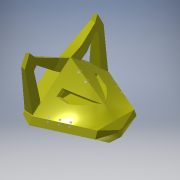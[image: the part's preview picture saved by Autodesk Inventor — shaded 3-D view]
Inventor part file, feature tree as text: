
AUTODESK INVENTOR PART (.ipt)
format: ipt  version: 2017 (Build 210142000, 142)  size: 774,144 bytes
history: native  units: in
note: dims shown in document units (in); Inventor stores cm internally (conversion verified against a paired STEP export)
features: sketch x22, extrude x16, plane x9, projected_geometry x5, loft x4, other x3, chamfer x1, mirror x1, emboss x1, fillet x1
ambient origin geometry x8: Origin, YZ Plane, XZ Plane, XY Plane, X Axis, Y Axis, Z Axis, Center Point
bodies: Solid1 (feature_tree)
feature tree (63):
  sketch  "Sketch1"  dims[d0=0.7559in d1=0.7559in]
  plane  "Work Plane1"
  loft  "Loft1"
  extrude  "Extrusion1"  Depth=0.2in
  plane  "Work Plane4"
  loft  "Loft2"
  plane  "Work Plane5"
  loft  "Loft3"
  loft  "Loft4"
  extrude  "Extrusion2"  TaperAngle=0.0deg  [1 undecoded]
  plane  "Work Plane6"
  extrude  "Extrusion3"  Depth=1.0in
  extrude  "Extrusion4"  Depth=1.0651in
  extrude  "Extrusion5"  Depth=0.962in
  plane  "Work Plane7"
  extrude  "Extrusion6"  Depth=0.075in
  plane  "Work Plane8"
  other  "Work Axis1"
  plane  "Work Plane9"
  chamfer  "Chamfer1"  Distance=0.45in
  extrude  "Extrusion7"  Depth=0.01in
  mirror  "Mirror3"
  extrude  "Extrusion8"  Depth=0.01in
  plane  "Work Plane10"
  extrude  "Extrusion9"  TaperAngle=0.0deg  [1 undecoded]
  plane  "Work Plane11"
  extrude  "Extrusion10"  Depth=0.07in
  extrude  "Extrusion11"  TaperAngle=0.0deg  [1 undecoded]
  extrude  "Extrusion12"  Depth=0.01in
  extrude  "Extrusion13"  TaperAngle=150.0deg  [1 undecoded]
  emboss  "Emboss1"
  extrude  "Extrusion16"  TaperAngle=150.0deg  [1 undecoded]
  extrude  "Extrusion17"  Depth=0.7in
  extrude  "Extrusion18"  Depth=0.05in
  fillet  "Fillet2"  Radius=0.05in
  sketch  "Sketch2"  dims[d2=0.9963in d3=0.2in]
  sketch  "Sketch3"  dims[d4=0.5in d6=0.08in]
  sketch  "Sketch4"  dims[d7=0.55in d8=150.0deg]
  other  "Edges1"
  sketch  "Sketch5"  dims[d9=150.0deg d14=0.33in]
  projected_geometry  "Projected Loop1"
  other  "Edges2"
  sketch  "Sketch6"  dims[d15=0.66in d18=0.0in d19=90.0deg]
  sketch  "Sketch7"  dims[d20=0.0in d21=90.0deg d22=1.0in]
  sketch  "Sketch8"  dims[d26=1.0651in d28=1.0651in]
  sketch  "Sketch9"  dims[d29=0.0in d30=0.962in]
  sketch  "Sketch10"  dims[d31=0.962in d32=0.075in]
  sketch  "Sketch11"  dims[d33=0.15in]
  sketch  "Sketch12"  dims[d34=0.06in]
  sketch  "Sketch13"  dims[d35=0.1in]
  projected_geometry  "Projected Loop2"
  projected_geometry  "Projected Loop3"
  sketch  "Sketch14"  dims[d36=0.05in d37=0.45in d38=0.0in]
  projected_geometry  "Projected Loop4"
  sketch  "Sketch15"  dims[d39=0.0625in d40=0.01in]
  sketch  "Sketch16"  dims[d41=0.075in d42=0.01in]
  sketch  "Sketch17"  dims[d43=0.0in d44=90.0deg d45=0.0in d46=90.0deg]
  sketch  "Sketch18"  dims[d47=0.2in d48=0.07in]
  sketch  "Sketch19"  dims[d49=0.0in d50=90.0deg d51=0.0in d52=90.0deg]
  sketch  "Sketch23"  dims[d53=0.01in d54=0.01in]
  projected_geometry  "Projected Loop6"
  sketch  "Sketch24"  dims[d55=0.0344in d56=150.0deg]
  sketch  "Sketch25"  dims[d57=60.0deg d58=150.0deg d59=0.7in d60=0.05in d61=0.05in d62=0.05in d63=0.05in d64=0.05in d65=0.01in d66=0.0in d67=90.0deg d68=0.0in d69=90.0deg d70=0.1in d71=0.4in d72=0.15in d73=0.05in d74=0.0in d75=0.02in d77=0.15in d78=0.02in d79=0.1in d80=0.1in d81=0.1in d82=0.02in d83=0.15in d84=0.05in d85=0.0in d86=0.045in d87=0.0in d88=0.025in d89=0.0in d90=0.02in d91=0.02in d92=0.005in d93=0.0in d94=90.0deg d95=0.4466in d96=1.0in d97=0.0in d98=1.0in d99=0.0in d100=0.6528in d101=0.0in d102=0.0in d103=1.0in d104=0.0in d106=90.0deg d107=1.0in d108=0.0in d109=1.65in d110=0.1in d111=0.1in d112=0.0in d113=0.1in d114=0.075in d115=0.0in d116=0.05in d117=0.0in d123=0.84in d124=0.8in d125=0.0in d126=0.0in d127=1.0in d128=0.0in d130=0.225in d131=-0.0206in d133=0.2125in d134=0.1125in d135=0.07in d136=0.1in d137=0.02in d138=0.125in d139=45.0deg]
note: 5 required parameter values undecoded (feature->parameter linkage not recoverable at this tier; creation-order binding heuristic only, values carry confidence <= 0.55)
